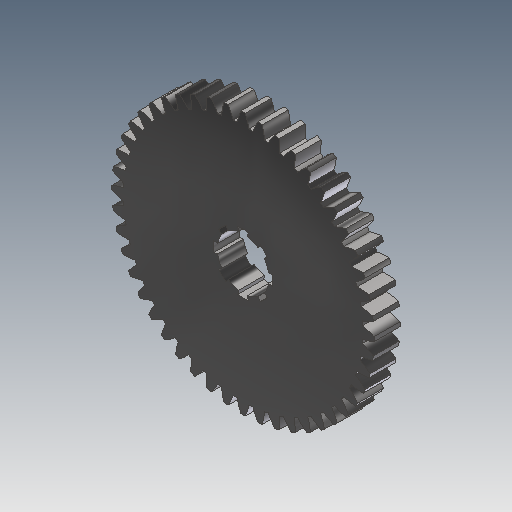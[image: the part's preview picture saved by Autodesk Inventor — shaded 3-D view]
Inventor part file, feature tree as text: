
AUTODESK INVENTOR PART (.ipt)
format: ipt  version: 2017 (Build 210142000, 142)  size: 381,952 bytes
history: native  units: mm (DEFAULTED — no unit token found)
features: extrude x3, plane x3, other x3, sketch x3, pattern_circular x1
ambient origin geometry x8: Origin, YZ Plane, XZ Plane, XY Plane, X Axis, Y Axis, Z Axis, Center Point
bodies: Solid1 (feature_tree)
feature tree (13):
  extrude  "Extrusion1"  Depth=1.0mm TaperAngle=0.0deg
  plane  "Work Plane2"
  plane  "Work Plane8"
  plane  "Work Plane9"
  other  "Цилиндрическое зубчатое зацепление"
  extrude  "Выдавливание2"  Depth=1.0mm
  extrude  "Выдавливание3"  Depth=10.0mm TaperAngle=0.0deg
  pattern_circular  "Круговой массив1"  [2 undecoded]
  sketch  "Sketch2"  dims[d0=10.116mm d1=1.0mm d2=0.0mm d3=9.762712mm d4=10.0mm d5=0.0mm d16=6.0mm d17=0.0mm d34=0.654498mm d39=0.0mm d41=0.0mm d43=6.0mm d46=6.0mm d47=0.0mm d48=0.0mm d49=2.0mm d50=10.0mm d51=0.0mm d52=2.3mm d53=3.490659mm d54=1.0mm d55=0.0mm d56=80.0mm d57=360.0deg]
  other  "Srf1"
  sketch  "Эскиз3"
  sketch  "Эскиз4"
  other  "Средний диаметр"
note: 2 required parameter values undecoded (feature->parameter linkage not recoverable at this tier; creation-order binding heuristic only, values carry confidence <= 0.55)
